# Revit family: Haworth_Kennedee_Sectional_Armless
name_source: partatom
category: Furniture
revit_build: Autodesk Revit 2018 (Build: 20170223_1515(x64)
units: mm (PartAtom-declared; Revit-internal decimal feet)

## family parameters
Always vertical = Yes
Cut with Voids When Loaded = No
OmniClass Number = 23.40.70.14.64.21
OmniClass Title = Systems Furniture
Room Calculation Point = No
Shared = No
Work Plane-Based = No

## types (2) — shared parameters
Assembly Code = E2020200
Base Finish = Haworth _ Paint _ Metallic Gunmetal
Description = Haworth Kennedee Sectional Armless
Leg Offset = 16 1/2"
Leg Thickness = 2"
Manufacturer = Haworth
Model = HCPF-KEK
Revision Number = 4
Size = Verify Final Dim. w/ Haworth
URL = http://www.haworth.com
URL - Product = http://www.haworth.com
Warranty = http://www.haworth.com

## per-type parameters (varying)
| type | Bench Width | One Seat | Two Seats |
| HCPF-KEK - One Seat | 35 1/2" | Yes | No |
| HCPF-KEK - Two Seats | 71" | No | Yes |

## geometry (parser evidence)
native form markers: Sweep x5
no freeform markers — native parametric forms only
